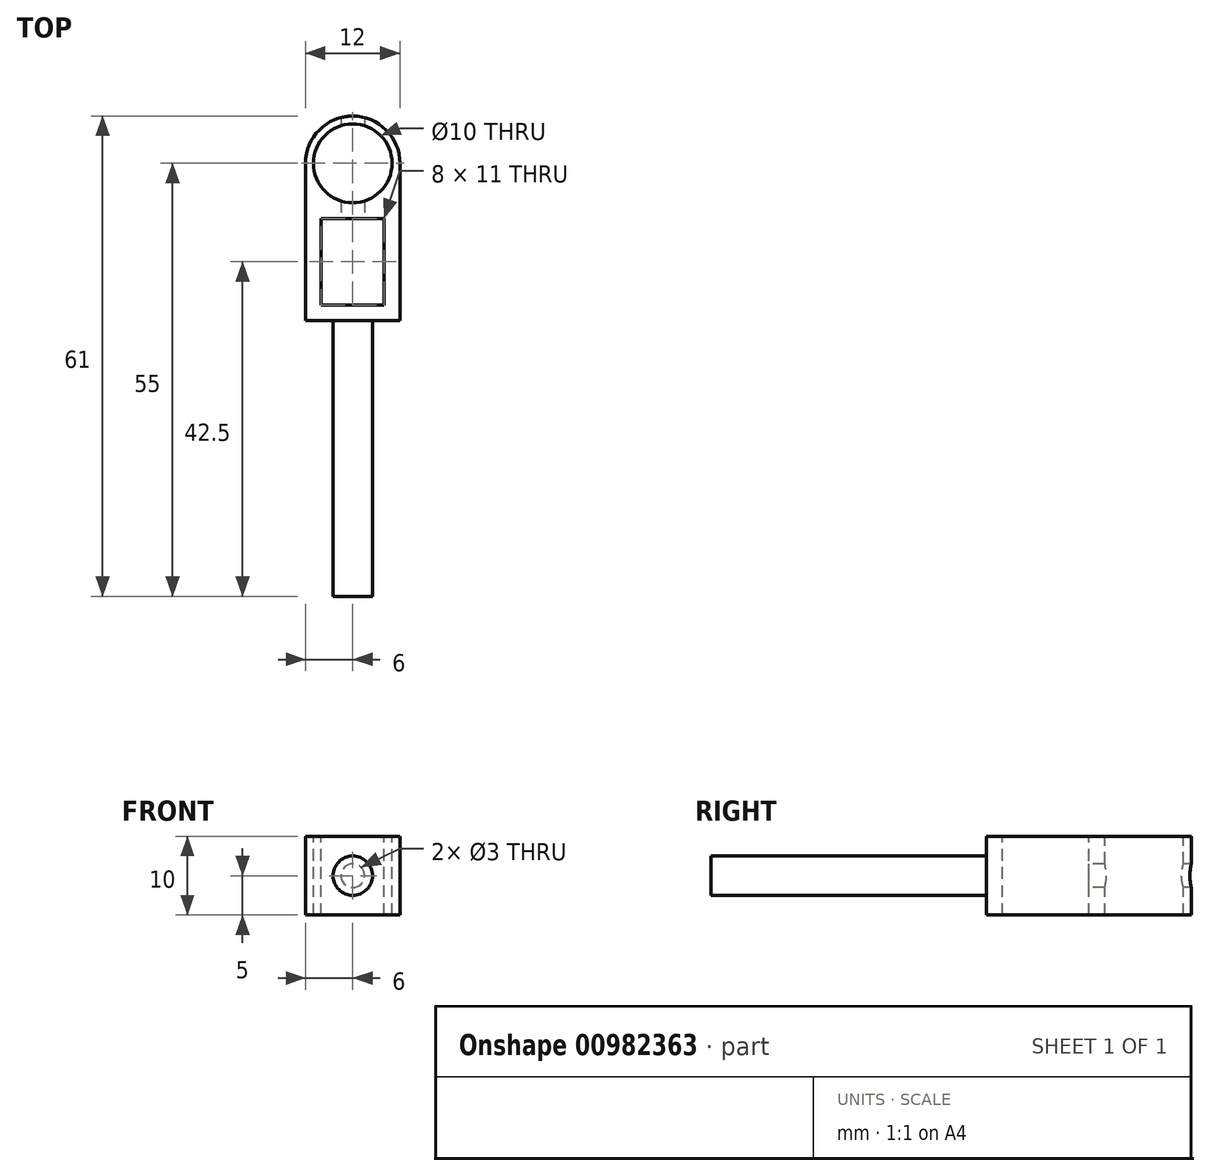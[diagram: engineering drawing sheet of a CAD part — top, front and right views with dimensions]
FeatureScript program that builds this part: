
annotation { "Feature Type Name" : "Feature", "Feature Type Description" : "" }
export const myFeature = defineFeature(function(context is Context, id is Id, definition is map)
    precondition{}
    {
        {
            var Q0;
            Q0=qCreatedBy(makeId("Top.planeOp"),FACE);
            var sketch = newSketch(context, id + "F0", { "sketchPlane" : qUnion([Q0])});
            skCircle(sketch, "E0", {"center": v(0, 0) * mm, "radius": 6 * mm});
            skLineSegment(sketch, "E1.bottom", {"start": v(-6, 0) * mm, "end": v(6, 0) * mm});
            skLineSegment(sketch, "E1.top", {"start": v(-6, -20) * mm, "end": v(6, -20) * mm});
            skLineSegment(sketch, "E1.left", {"start": v(-6, 0) * mm, "end": v(-6, -20) * mm});
            skLineSegment(sketch, "E1.right", {"start": v(6, 0) * mm, "end": v(6, -20) * mm});
            skSolve(sketch);
        }
        {
            var Q0;
            {var subQ0=sQuery(id+"F0.wireOp",EDGE,"E1.bottom");var subQ1=sQuery(id+"F0.wireOp",EDGE,"E0");var subQ3=makeQuery(id+"F0.imprint","INTERSECT",VERTEX,{"derivedFrom":[subQ1,subQ0]});Q0=makeQuery(id+"F0.imprint","IMPRINT",FACE,{"disambiguationData":[TD([[makeQuery(id+"F0.imprint","IMPRINT",EDGE,{"disambiguationData":[TD([[subQ3,1.0]])],"derivedFrom":subQ1}),1.0]])]});}
            var Q1;
            {var subQ0=sQuery(id+"F0.wireOp",EDGE,"E1.bottom");var subQ1=sQuery(id+"F0.wireOp",EDGE,"E0");var subQ3=makeQuery(id+"F0.imprint","INTERSECT",VERTEX,{"derivedFrom":[subQ1,subQ0]});Q1=makeQuery(id+"F0.imprint","IMPRINT",FACE,{"disambiguationData":[TD([[makeQuery(id+"F0.imprint","IMPRINT",EDGE,{"disambiguationData":[TD([[subQ3,-1.0]])],"derivedFrom":subQ1}),1.0]])]});}
            var Q2;
            Q2=makeQuery(id+"F0.imprint","IMPRINT",FACE,{"disambiguationData":[TD([[makeQuery(id+"F0.imprint","IMPRINT",EDGE,{"derivedFrom":sQuery(id+"F0.wireOp",EDGE,"E1.top")}),1.0]])]});
            extrude(context, id + "F1", {"entities" : qUnion([Q0, Q1, Q2]), "depth" : 10 * mm, "offsetDistance" : 25 * mm});
        }
        {
            var Q0;
            Q0=makeQuery(id+"F1.opExtrude","CAP_FACE",FACE,{"disambiguationData":[OSD([sQuery(id+"F0.wireOp",EDGE,"E0"),sQuery(id+"F0.wireOp",EDGE,"E1.bottom"),sQuery(id+"F0.wireOp",EDGE,"E1.top"),sQuery(id+"F0.wireOp",EDGE,"E1.left"),sQuery(id+"F0.wireOp",EDGE,"E1.right")])],"isStart":false});
            var sketch = newSketch(context, id + "F2", { "sketchPlane" : qUnion([Q0])});
            skCircle(sketch, "E2", {"center": v(0, 0) * mm, "radius": 5 * mm});
            skSolve(sketch);
        }
        {
            var Q0;
            Q0=makeQuery(id+"F2.imprint","IMPRINT",FACE,{"disambiguationData":[TD([[makeQuery(id+"F2.imprint","IMPRINT",EDGE,{"derivedFrom":sQuery(id+"F2.wireOp",EDGE,"E2")}),1.0]])]});
            extrude(context, id + "F3", {"entities" : qUnion([Q0]), "operationType" : NewBodyOperationType.REMOVE, "oppositeDirection" : true, "depth" : 25 * mm, "offsetDistance" : 25 * mm});
        }
        {
            var Q0;
            Q0=makeQuery(id+"F1.opExtrude","CAP_FACE",FACE,{"disambiguationData":[OSD([sQuery(id+"F0.wireOp",EDGE,"E0"),sQuery(id+"F0.wireOp",EDGE,"E1.bottom"),sQuery(id+"F0.wireOp",EDGE,"E1.top"),sQuery(id+"F0.wireOp",EDGE,"E1.left"),sQuery(id+"F0.wireOp",EDGE,"E1.right")])],"isStart":false});
            var sketch = newSketch(context, id + "F4", { "sketchPlane" : qUnion([Q0])});
            skLineSegment(sketch, "E3.bottom", {"start": v(-6, -20) * mm, "end": v(-4, -20) * mm});
            skLineSegment(sketch, "E3.top", {"start": v(-6, -18) * mm, "end": v(-4, -18) * mm});
            skLineSegment(sketch, "E3.left", {"start": v(-6, -20) * mm, "end": v(-6, -18) * mm});
            skLineSegment(sketch, "E3.right", {"start": v(-4, -20) * mm, "end": v(-4, -18) * mm});
            skLineSegment(sketch, "E4.bottom", {"start": v(6, -20) * mm, "end": v(4, -20) * mm});
            skLineSegment(sketch, "E4.top", {"start": v(6, -18) * mm, "end": v(4, -18) * mm});
            skLineSegment(sketch, "E4.left", {"start": v(6, -20) * mm, "end": v(6, -18) * mm});
            skLineSegment(sketch, "E4.right", {"start": v(4, -20) * mm, "end": v(4, -18) * mm});
            skLineSegment(sketch, "E5.left", {"start": v(6, -18) * mm, "end": v(6, -18) * mm});
            skLineSegment(sketch, "E5.right", {"start": v(4, -18) * mm, "end": v(4, -18) * mm});
            skLineSegment(sketch, "E6.bottom", {"start": v(4, -18) * mm, "end": v(6, -18) * mm});
            skLineSegment(sketch, "E6.top", {"start": v(4, -18) * mm, "end": v(6, -18) * mm});
            skLineSegment(sketch, "E7", {"start": v(0, -5) * mm, "end": v(0, -7) * mm});
            skLineSegment(sketch, "E8.bottom", {"start": v(-4, -18) * mm, "end": v(4, -18) * mm});
            skLineSegment(sketch, "E8.top", {"start": v(-4, -7) * mm, "end": v(4, -7) * mm});
            skLineSegment(sketch, "E8.left", {"start": v(-4, -18) * mm, "end": v(-4, -7) * mm});
            skLineSegment(sketch, "E8.right", {"start": v(4, -18) * mm, "end": v(4, -7) * mm});
            skSolve(sketch);
        }
        {
            var Q0;
            Q0=makeQuery(id+"F4.imprint","IMPRINT",FACE,{"disambiguationData":[TD([[makeQuery(id+"F4.imprint","IMPRINT",EDGE,{"derivedFrom":sQuery(id+"F4.wireOp",EDGE,"E8.bottom")}),1.0]])]});
            extrude(context, id + "F5", {"entities" : qUnion([Q0]), "operationType" : NewBodyOperationType.REMOVE, "oppositeDirection" : true, "depth" : 25 * mm, "offsetDistance" : 25 * mm});
        }
        {
            var Q0;
            Q0=makeQuery(id+"F5.boolean.opBoolean","COPY",FACE,{"derivedFrom":makeQuery(id+"F5.opExtrude","SWEPT_FACE",FACE,{"disambiguationData":[OSD([sQuery(id+"F4.wireOp",EDGE,"E8.top")])]})});
            var sketch = newSketch(context, id + "F6", { "sketchPlane" : qUnion([Q0])});
            skLineSegment(sketch, "E9", {"start": v(0, 10) * mm, "end": v(0, 5) * mm, "construction": true});
            skCircle(sketch, "E10", {"center": v(0, 5) * mm, "radius": 1.5 * mm});
            skSolve(sketch);
        }
        {
            var Q0;
            Q0 = qSketchRegion(id + "F6", true);
            extrude(context, id + "F7", {"entities" : qUnion([Q0]), "operationType" : NewBodyOperationType.REMOVE, "oppositeDirection" : true, "depth" : 25 * mm, "offsetDistance" : 25 * mm});
        }
        {
            var Q0;
            Q0=makeQuery(id+"F1.opExtrude","SWEPT_FACE",FACE,{"disambiguationData":[OSD([sQuery(id+"F0.wireOp",EDGE,"E1.top")])]});
            var sketch = newSketch(context, id + "F8", { "sketchPlane" : qUnion([Q0])});
            skCircle(sketch, "E11", {"center": v(0, 5) * mm, "radius": 2.5 * mm});
            skPoint(sketch, "E11.centerSnap0", {"position": v(-6, 5) * mm});
            skSolve(sketch);
        }
        {
            var Q0;
            Q0 = qSketchRegion(id + "F8", true);
            extrude(context, id + "F9", {"entities" : qUnion([Q0]), "operationType" : NewBodyOperationType.ADD, "depth" : 35 * mm, "offsetDistance" : 25 * mm});
        }
    });
